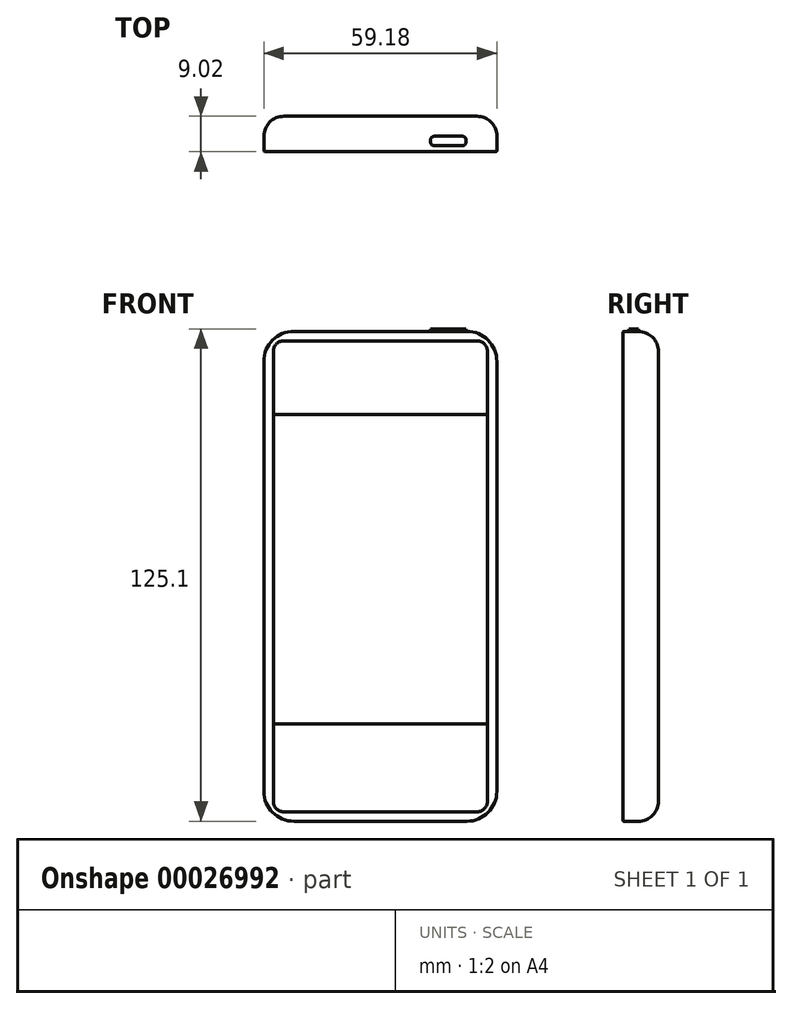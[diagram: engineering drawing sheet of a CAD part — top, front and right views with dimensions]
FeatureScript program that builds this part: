
annotation { "Feature Type Name" : "Feature", "Feature Type Description" : "" }
export const myFeature = defineFeature(function(context is Context, id is Id, definition is map)
    precondition{}
    {
        {
            var Q0;
            Q0=qCreatedBy(makeId("Front.planeOp"),FACE);
            var sketch = newSketch(context, id + "F0", { "sketchPlane" : qUnion([Q0])});
            skLineSegment(sketch, "E0.bottom", {"start": v(-42.34, 80.42) * mm, "end": v(16.84, 80.42) * mm});
            skLineSegment(sketch, "E0.top", {"start": v(-42.34, -44.04) * mm, "end": v(16.84, -44.04) * mm});
            skLineSegment(sketch, "E0.left", {"start": v(-42.34, 80.42) * mm, "end": v(-42.34, -44.04) * mm});
            skLineSegment(sketch, "E0.right", {"start": v(16.84, 80.42) * mm, "end": v(16.84, -44.04) * mm});
            skSolve(sketch);
        }
        {
            var Q0;
            Q0=makeQuery(id+"F0.imprint","IMPRINT",FACE,{"disambiguationData":[TD([[makeQuery(id+"F0.imprint","IMPRINT",EDGE,{"derivedFrom":sQuery(id+"F0.wireOp",EDGE,"E0.bottom")}),-1.0]])]});
            extrude(context, id + "F1", {"entities" : qUnion([Q0]), "depth" : 8.97 * mm});
        }
        {
            var Q0;
            Q0=makeQuery(id+"F1.opExtrude","SWEPT_EDGE",EDGE,{"disambiguationData":[OSD([sQuery(id+"F0.wireOp",EDGE,"E0.bottom"),sQuery(id+"F0.wireOp",EDGE,"E0.left")])]});
            var Q1;
            Q1=makeQuery(id+"F1.opExtrude","SWEPT_EDGE",EDGE,{"disambiguationData":[OSD([sQuery(id+"F0.wireOp",EDGE,"E0.bottom"),sQuery(id+"F0.wireOp",EDGE,"E0.right")])]});
            var Q2;
            Q2=makeQuery(id+"F1.opExtrude","SWEPT_EDGE",EDGE,{"disambiguationData":[OSD([sQuery(id+"F0.wireOp",EDGE,"E0.top"),sQuery(id+"F0.wireOp",EDGE,"E0.left")])]});
            var Q3;
            Q3=makeQuery(id+"F1.opExtrude","SWEPT_EDGE",EDGE,{"disambiguationData":[OSD([sQuery(id+"F0.wireOp",EDGE,"E0.top"),sQuery(id+"F0.wireOp",EDGE,"E0.right")])]});
            fillet(context, id + "F2", {"entities" : qUnion([Q0, Q1, Q2, Q3]), "radius" : 7.62 * mm, "tangentPropagation" : true, "allowEdgeOverflow" : false});
        }
        {
            var Q0;
            Q0=makeQuery(id+"F1.opExtrude","CAP_EDGE",EDGE,{"disambiguationData":[OSD([sQuery(id+"F0.wireOp",EDGE,"E0.right")])],"isStart":true});
            fillet(context, id + "F3", {"entities" : qUnion([Q0]), "radius" : 5.08 * mm, "tangentPropagation" : true, "allowEdgeOverflow" : false});
        }
        {
            var Q0;
            Q0=makeQuery(id+"F1.opExtrude","CAP_EDGE",EDGE,{"disambiguationData":[OSD([sQuery(id+"F0.wireOp",EDGE,"E0.left")])],"isStart":false});
            var Q1;
            Q1=makeQuery(id+"F1.opExtrude","CAP_EDGE",EDGE,{"disambiguationData":[OSD([sQuery(id+"F0.wireOp",EDGE,"E0.bottom")])],"isStart":false});
            var Q2;
            Q2=makeQuery(id+"F1.opExtrude","CAP_EDGE",EDGE,{"disambiguationData":[OSD([sQuery(id+"F0.wireOp",EDGE,"E0.right")])],"isStart":false});
            var Q3;
            Q3=makeQuery(id+"F1.opExtrude","CAP_EDGE",EDGE,{"disambiguationData":[OSD([sQuery(id+"F0.wireOp",EDGE,"E0.top")])],"isStart":false});
            fillet(context, id + "F4", {"entities" : qUnion([Q0, Q1, Q2, Q3]), "radius" : 0.25 * mm, "tangentPropagation" : true, "allowEdgeOverflow" : false});
        }
        {
            var Q0;
            Q0=makeQuery(id+"F1.opExtrude","CAP_FACE",FACE,{"disambiguationData":[OSD([sQuery(id+"F0.wireOp",EDGE,"E0.bottom"),sQuery(id+"F0.wireOp",EDGE,"E0.top"),sQuery(id+"F0.wireOp",EDGE,"E0.left"),sQuery(id+"F0.wireOp",EDGE,"E0.right")])],"isStart":false});
            var sketch = newSketch(context, id + "F5", { "sketchPlane" : qUnion([Q0])});
            skLineSegment(sketch, "E1.bottom", {"start": v(-37.4, 78) * mm, "end": v(11.89, 78) * mm});
            skLineSegment(sketch, "E1.top", {"start": v(-37.4, -41.63) * mm, "end": v(11.89, -41.63) * mm});
            skLineSegment(sketch, "E1.left", {"start": v(-39.93, 75.47) * mm, "end": v(-39.93, -39.09) * mm});
            skLineSegment(sketch, "E1.right", {"start": v(14.43, 75.47) * mm, "end": v(14.43, -39.09) * mm});
            skPoint(sketch, "E2.visualSharp", {"position": v(-39.93, 78) * mm});
            skArc(sketch, "E2.filletArc", {"start": v(-37.4, 78) * mm, "mid": v(-39.19, 77.26) * mm, "end": v(-39.93, 75.47) * mm});
            skPoint(sketch, "E3.visualSharp", {"position": v(-39.93, -41.63) * mm});
            skArc(sketch, "E3.filletArc", {"start": v(-39.93, -39.09) * mm, "mid": v(-39.19, -40.88) * mm, "end": v(-37.4, -41.63) * mm});
            skPoint(sketch, "E4.visualSharp", {"position": v(14.43, -41.63) * mm});
            skArc(sketch, "E4.filletArc", {"start": v(11.89, -41.63) * mm, "mid": v(13.68, -40.88) * mm, "end": v(14.43, -39.09) * mm});
            skPoint(sketch, "E5.visualSharp", {"position": v(14.43, 78) * mm});
            skArc(sketch, "E5.filletArc", {"start": v(14.43, 75.47) * mm, "mid": v(13.68, 77.26) * mm, "end": v(11.89, 78) * mm});
            skSolve(sketch);
        }
        {
            var Q0;
            Q0 = qSketchRegion(id + "F5", true);
            extrude(context, id + "F6", {"entities" : qUnion([Q0]), "depth" : 0.03 * mm});
        }
        {
            var Q0;
            Q0=makeQuery(id+"F6.opExtrude","CAP_FACE",FACE,{"disambiguationData":[OSD([sQuery(id+"F5.wireOp",EDGE,"E1.bottom"),sQuery(id+"F5.wireOp",EDGE,"E1.top"),sQuery(id+"F5.wireOp",EDGE,"E1.left"),sQuery(id+"F5.wireOp",EDGE,"E1.right"),sQuery(id+"F5.wireOp",EDGE,"E2.filletArc"),sQuery(id+"F5.wireOp",EDGE,"E3.filletArc"),sQuery(id+"F5.wireOp",EDGE,"E4.filletArc"),sQuery(id+"F5.wireOp",EDGE,"E5.filletArc")])],"isStart":false});
            var sketch = newSketch(context, id + "F7", { "sketchPlane" : qUnion([Q0])});
            skLineSegment(sketch, "E6.bottom", {"start": v(-39.93, 59.36) * mm, "end": v(14.43, 59.36) * mm});
            skLineSegment(sketch, "E6.top", {"start": v(-39.93, -19.28) * mm, "end": v(14.43, -19.28) * mm});
            skLineSegment(sketch, "E6.left", {"start": v(-39.93, 59.36) * mm, "end": v(-39.93, -19.28) * mm});
            skLineSegment(sketch, "E6.right", {"start": v(14.43, 59.36) * mm, "end": v(14.43, -19.28) * mm});
            skSolve(sketch);
        }
        {
            var Q0;
            Q0 = qSketchRegion(id + "F7", true);
            extrude(context, id + "F8", {"entities" : qUnion([Q0]), "operationType" : NewBodyOperationType.ADD, "depth" : 0.03 * mm});
        }
        {
            var Q0;
            Q0=makeQuery(id+"F1.opExtrude","SWEPT_FACE",FACE,{"disambiguationData":[OSD([sQuery(id+"F0.wireOp",EDGE,"E0.bottom")])]});
            var sketch = newSketch(context, id + "F9", { "sketchPlane" : qUnion([Q0])});
            skLineSegment(sketch, "E7.bottom", {"start": v(1.02, -5.08) * mm, "end": v(8.04, -5.08) * mm});
            skLineSegment(sketch, "E7.top", {"start": v(1.02, -7.5) * mm, "end": v(8.04, -7.5) * mm});
            skLineSegment(sketch, "E7.left", {"start": v(0, -6.1) * mm, "end": v(0, -6.48) * mm});
            skLineSegment(sketch, "E7.right", {"start": v(9.06, -6.1) * mm, "end": v(9.06, -6.48) * mm});
            skPoint(sketch, "E8.visualSharp", {"position": v(0, -5.08) * mm});
            skArc(sketch, "E8.filletArc", {"start": v(1.02, -5.08) * mm, "mid": v(0.3, -5.38) * mm, "end": v(0, -6.1) * mm});
            skPoint(sketch, "E9.visualSharp", {"position": v(0, -7.5) * mm});
            skArc(sketch, "E9.filletArc", {"start": v(0, -6.48) * mm, "mid": v(0.3, -7.2) * mm, "end": v(1.02, -7.5) * mm});
            skPoint(sketch, "E10.visualSharp", {"position": v(9.06, -5.08) * mm});
            skArc(sketch, "E10.filletArc", {"start": v(9.06, -6.1) * mm, "mid": v(8.76, -5.38) * mm, "end": v(8.04, -5.08) * mm});
            skPoint(sketch, "E11.visualSharp", {"position": v(9.06, -7.5) * mm});
            skArc(sketch, "E11.filletArc", {"start": v(8.04, -7.5) * mm, "mid": v(8.76, -7.2) * mm, "end": v(9.06, -6.48) * mm});
            skSolve(sketch);
        }
        {
            var Q0;
            Q0=makeQuery(id+"F9.imprint","IMPRINT",FACE,{"disambiguationData":[TD([[makeQuery(id+"F9.imprint","IMPRINT",EDGE,{"derivedFrom":sQuery(id+"F9.wireOp",EDGE,"E7.bottom")}),1.0]])]});
            extrude(context, id + "F10", {"entities" : qUnion([Q0]), "operationType" : NewBodyOperationType.ADD, "depth" : 0.64 * mm});
        }
    });
